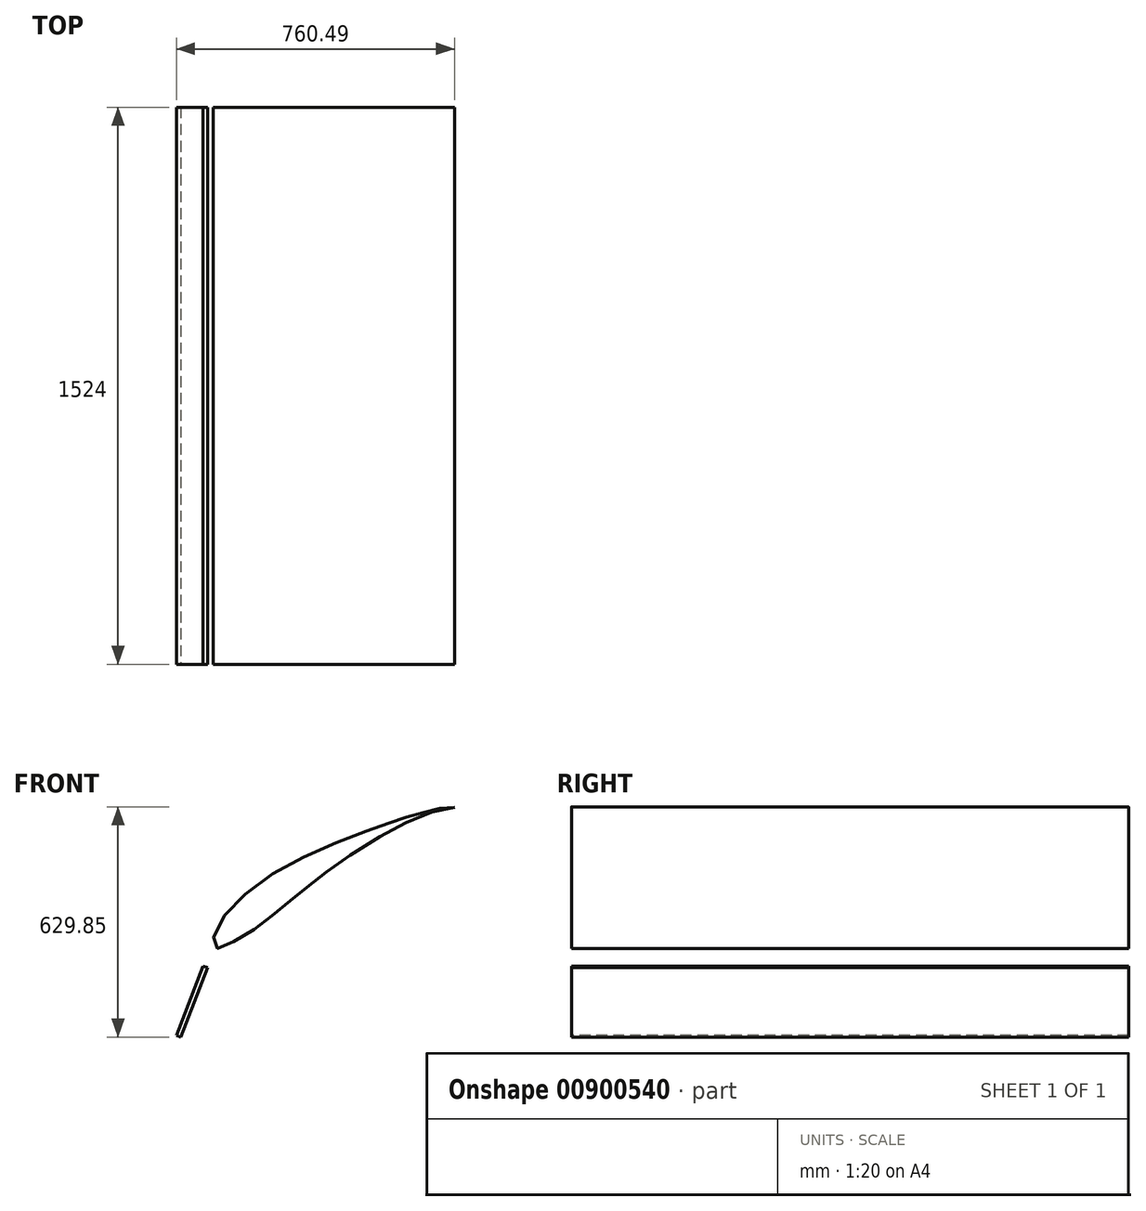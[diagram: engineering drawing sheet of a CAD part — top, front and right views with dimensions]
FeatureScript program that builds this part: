
annotation { "Feature Type Name" : "Feature", "Feature Type Description" : "" }
export const myFeature = defineFeature(function(context is Context, id is Id, definition is map)
    precondition{}
    {
        {
            var Q0;
            Q0=qCreatedBy(makeId("Front.planeOp"),FACE);
            var sketch = newSketch(context, id + "F0", { "sketchPlane" : qUnion([Q0])});
            skLineSegment(sketch, "E0", {"start": v(-364.38, -8.9) * mm, "end": v(397.62, -8.9) * mm});
            skFitSpline(sketch, "E1", {"points": [v(748.63, 627.9) * mm, v(731.83, 626.36) * mm, v(705.83, 621.18) * mm, v(677.55, 612.12) * mm, v(645.57, 599.93) * mm, v(612.45, 584.84) * mm, v(583.84, 569.98) * mm, v(547.2, 550.06) * mm, v(503.33, 523.65) * mm, v(454.05, 491.47) * mm, v(422.6, 468.94) * mm, v(398.7, 451.2) * mm, v(368.62, 428.03) * mm, v(353.67, 416) * mm, v(335.88, 402.45) * mm, v(315.05, 385.82) * mm, v(305.57, 378) * mm, v(289.5, 364.7) * mm, v(267.88, 347.46) * mm, v(251.24, 333.55) * mm, v(236.13, 321.51) * mm, v(216.33, 306.3) * mm, v(198.08, 293.5) * mm, v(176.38, 279.8) * mm, v(163.3, 271.9) * mm, v(130.85, 254.03) * mm, v(118.6, 248.32) * mm, v(109.98, 244.97) * mm, v(102.94, 243.18) * mm, v(96.7, 242.84) * mm, v(92.47, 245.54) * mm, v(90.79, 247.56) * mm, v(88.86, 253.15) * mm, v(88.18, 264.93) * mm, v(91.25, 281.47) * mm, v(98.46, 300.22) * mm, v(117.36, 329.48) * mm, v(137.06, 353.1) * mm, v(169.94, 385.42) * mm, v(206.3, 415.33) * mm, v(251.32, 446.6) * mm, v(289.83, 468.96) * mm, v(349.8, 498.44) * mm, v(407.66, 524.16) * mm, v(438.67, 536.86) * mm, v(487.59, 555.73) * mm, v(523, 568.9) * mm, v(545.32, 576.7) * mm, v(565.4, 584.2) * mm, v(584.85, 590.86) * mm, v(597.8, 595.02) * mm, v(609.46, 598.63) * mm, v(623.19, 603.04) * mm, v(635.9, 606.73) * mm, v(653.22, 611.79) * mm, v(663.72, 614.79) * mm, v(671.13, 616.72) * mm, v(684.66, 620.24) * mm, v(696.67, 623.33) * mm, v(711.28, 626.43) * mm, v(724.32, 628.88) * mm, v(732.26, 629.56) * mm, v(741.44, 629.66) * mm, v(748.63, 627.9) * mm]});
            skSolve(sketch);
        }
        {
            var Q0;
            Q0=qCreatedBy(makeId("Front.planeOp"),FACE);
            var sketch = newSketch(context, id + "F1", { "sketchPlane" : qUnion([Q0])});
            skLineSegment(sketch, "E2.bottom", {"start": v(-11.86, 4.54) * mm, "end": v(60.71, 194.33) * mm});
            skLineSegment(sketch, "E2.top", {"start": v(0, 0) * mm, "end": v(72.58, 189.8) * mm});
            skLineSegment(sketch, "E2.left", {"start": v(-11.86, 4.54) * mm, "end": v(0, 0) * mm});
            skLineSegment(sketch, "E2.right", {"start": v(60.71, 194.33) * mm, "end": v(72.58, 189.8) * mm});
            skSolve(sketch);
        }
        {
            var Q0;
            Q0=makeQuery(id+"F1.imprint","IMPRINT",FACE,{"disambiguationData":[TD([[makeQuery(id+"F1.imprint","IMPRINT",EDGE,{"derivedFrom":sQuery(id+"F1.wireOp",EDGE,"E2.bottom")}),-1.0]])]});
            var Q1;
            Q1=makeQuery(id+"F0.imprint","IMPRINT",FACE,{"disambiguationData":[TD([[makeQuery(id+"F0.imprint","IMPRINT",EDGE,{"derivedFrom":sQuery(id+"F0.wireOp",EDGE,"E1")}),-1.0]])]});
            extrude(context, id + "F2", {"entities" : qUnion([Q0, Q1]), "oppositeDirection" : true, "depth" : 1524 * mm, "offsetDistance" : 25.4 * mm});
        }
    });
